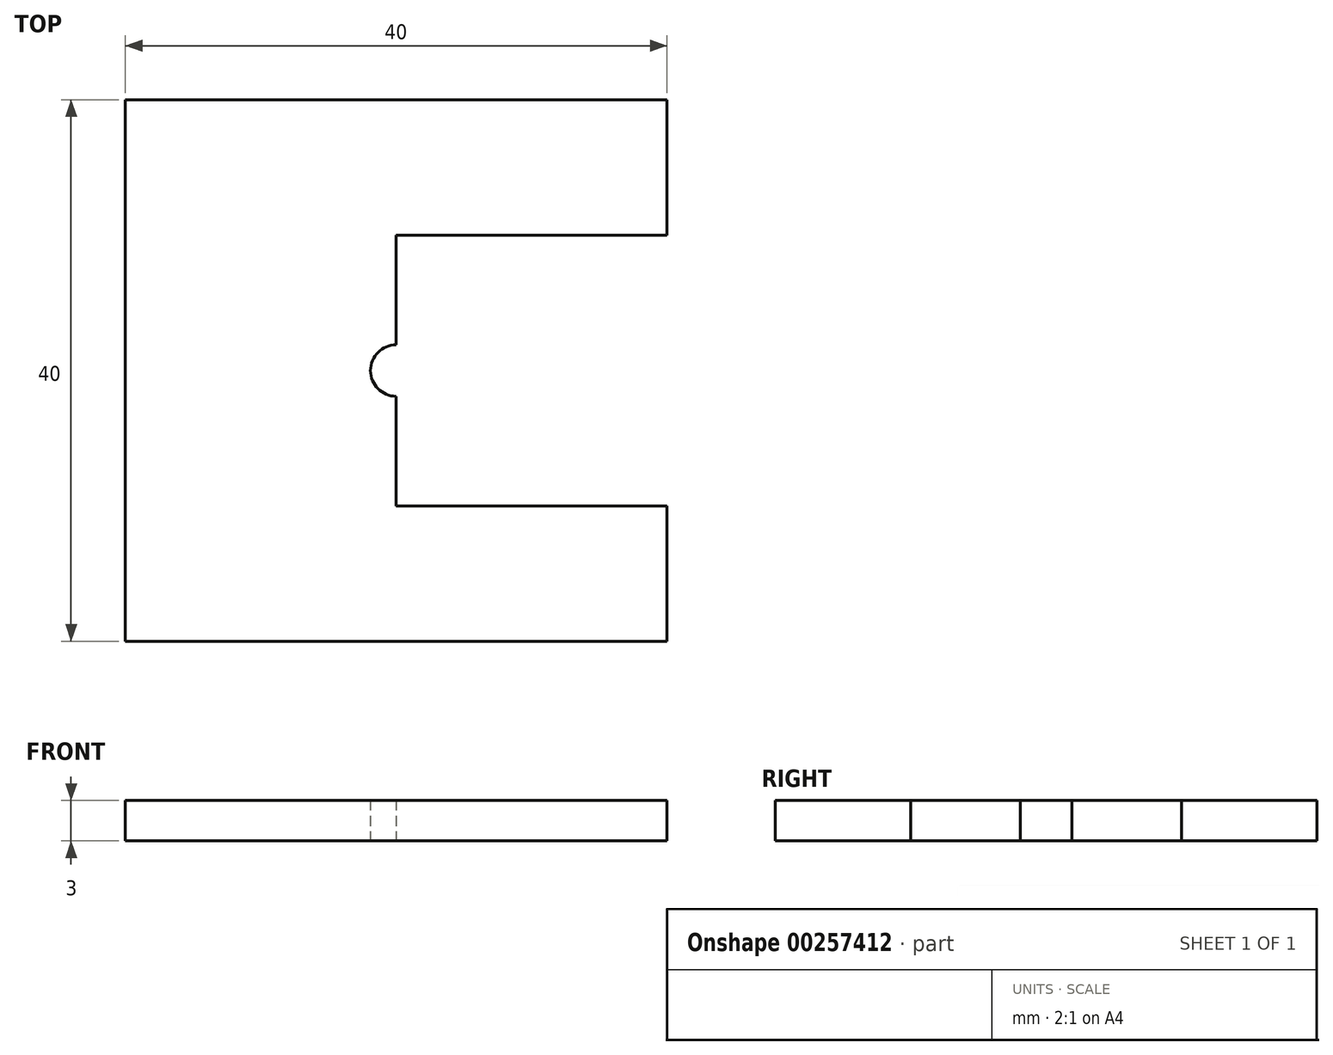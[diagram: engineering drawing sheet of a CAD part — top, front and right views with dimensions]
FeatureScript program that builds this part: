
annotation { "Feature Type Name" : "Feature", "Feature Type Description" : "" }
export const myFeature = defineFeature(function(context is Context, id is Id, definition is map)
    precondition{}
    {
        {
            var Q0;
            Q0=qCreatedBy(makeId("Top.planeOp"),FACE);
            var sketch = newSketch(context, id + "F0", { "sketchPlane" : qUnion([Q0])});
            skLineSegment(sketch, "E0.bottom", {"start": v(-20, 20) * mm, "end": v(20, 20) * mm});
            skLineSegment(sketch, "E0.top", {"start": v(-20, -20) * mm, "end": v(20, -20) * mm});
            skLineSegment(sketch, "E0.left", {"start": v(-20, 20) * mm, "end": v(-20, -20) * mm});
            skLineSegment(sketch, "E0.right", {"start": v(20, 20) * mm, "end": v(20, 10) * mm});
            skPoint(sketch, "E0.middle", {"position": v(0, 0) * mm});
            skArc(sketch, "E1", {"start": v(0, 1.9) * mm, "mid": v(-1.9, 0) * mm, "end": v(0, -1.9) * mm});
            skLineSegment(sketch, "E2", {"start": v(0, 10) * mm, "end": v(20, 10) * mm});
            skLineSegment(sketch, "E3", {"start": v(0, -10) * mm, "end": v(20, -10) * mm});
            skLineSegment(sketch, "E4", {"start": v(0, 10) * mm, "end": v(0, 1.9) * mm});
            skLineSegment(sketch, "E5", {"start": v(0, -10) * mm, "end": v(0, -1.9) * mm});
            skLineSegment(sketch, "E6.trimOffspring", {"start": v(20, -10) * mm, "end": v(20, -20) * mm});
            skSolve(sketch);
        }
        {
            var Q0;
            Q0 = qSketchRegion(id + "F0", true);
            extrude(context, id + "F1", {"entities" : qUnion([Q0]), "depth" : 3 * mm});
        }
    });
